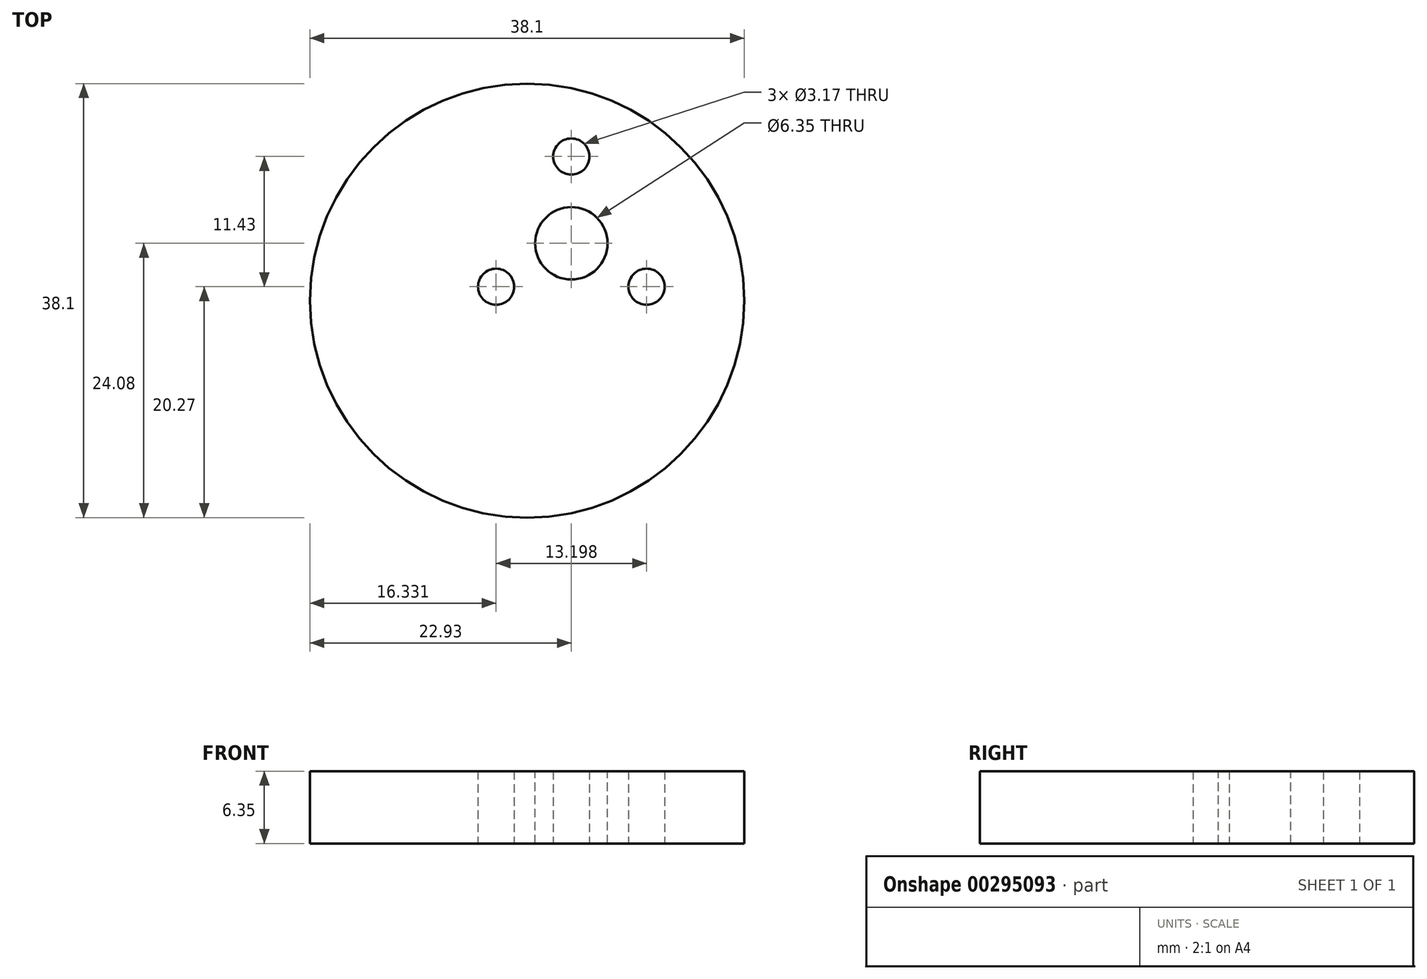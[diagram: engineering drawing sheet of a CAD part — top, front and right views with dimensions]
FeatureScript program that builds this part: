
annotation { "Feature Type Name" : "Feature", "Feature Type Description" : "" }
export const myFeature = defineFeature(function(context is Context, id is Id, definition is map)
    precondition{}
    {
        {
            var Q0;
            Q0=qCreatedBy(makeId("Top.planeOp"),FACE);
            var sketch = newSketch(context, id + "F0", { "sketchPlane" : qUnion([Q0])});
            skCircle(sketch, "E0", {"center": v(0, 7.62) * mm, "radius": 1.59 * mm});
            skCircle(sketch, "E1.1.0", {"center": v(-6.6, -3.81) * mm, "radius": 1.59 * mm});
            skCircle(sketch, "E1.2.0", {"center": v(6.6, -3.8) * mm, "radius": 1.59 * mm});
            skPoint(sketch, "E1.center", {"position": v(0, 0) * mm});
            skLineSegment(sketch, "E1.anchor1", {"start": v(0, 0) * mm, "end": v(0, 7.62) * mm, "construction": true});
            skLineSegment(sketch, "E1.anchor2", {"start": v(0, 0) * mm, "end": v(6.6, -3.8) * mm, "construction": true});
            skCircle(sketch, "E2", {"center": v(-3.88, -5.03) * mm, "radius": 19.05 * mm});
            skSolve(sketch);
        }
        {
            var Q0;
            Q0=makeQuery(id+"F0.imprint","IMPRINT",FACE,{"disambiguationData":[TD([[makeQuery(id+"F0.imprint","IMPRINT",EDGE,{"derivedFrom":sQuery(id+"F0.wireOp",EDGE,"E0")}),-1.0]])]});
            extrude(context, id + "F1", {"entities" : qUnion([Q0]), "depth" : 6.35 * mm});
        }
        {
            var Q0;
            Q0=makeQuery(id+"F1.opExtrude","CAP_FACE",FACE,{"disambiguationData":[OSD([sQuery(id+"F0.wireOp",EDGE,"E0"),sQuery(id+"F0.wireOp",EDGE,"E1.1.0"),sQuery(id+"F0.wireOp",EDGE,"E1.2.0"),sQuery(id+"F0.wireOp",EDGE,"E2")])],"isStart":false});
            var sketch = newSketch(context, id + "F2", { "sketchPlane" : qUnion([Q0])});
            skPoint(sketch, "E3", {"position": v(0, 0) * mm});
            skSolve(sketch);
        }
        {
            var Q0;
            Q0=sQuery(id+"F2.wireOp",VERTEX,"E3");
            var Q1;
            Q1=makeQuery(id+"F1.opExtrude","SWEPT_BODY",BODY,{"disambiguationData":[OSD([sQuery(id+"F0.wireOp",EDGE,"E0"),sQuery(id+"F0.wireOp",EDGE,"E1.1.0"),sQuery(id+"F0.wireOp",EDGE,"E1.2.0"),sQuery(id+"F0.wireOp",EDGE,"E2")])]});
            hole(context, id + "F3", {"style" : HoleStyle.SIMPLE, "endStyle" : HoleEndStyle.THROUGH, "holeDiameter" : 6.35 * mm, "tappedDepth" : 12.7 * mm, "tapClearance" : 3, "locations" : qUnion([Q0]), "scope" : qUnion([Q1])});
        }
    });
